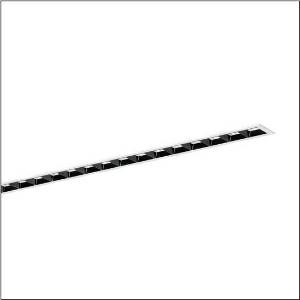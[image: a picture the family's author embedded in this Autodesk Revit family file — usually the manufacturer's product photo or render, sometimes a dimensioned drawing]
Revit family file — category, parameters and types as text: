
# Revit family: silica_r__21_51mx12tctaw_2b1a
name_source: partatom
category: Lighting Fixtures
units: mm (PartAtom-declared; Revit-internal decimal feet)

## family parameters
Cut with Voids When Loaded = No
Host = Face
Light Source = No
Part Type = Normal
Room Calculation Point = No
Round Connector Dimension = Use Diameter
Shared = No

## types (1)
- --- (1 x LED, 9300 lm, 80.4 W, 6500K)
    Apparent Load = 80 VA
    CIE Flux Codes = 84 100 100 100 100
    Color Rendering = 80
    Color Temperature = 6500K
    Default Elevation = 1800 mm
    Description = Silica® 21, office luminaire, primary light control with darklight reflector, of PMMA, black, CAT 2 (L<= 3000cd/m²), light emission: direct distribution, primary light characteristic: symmetric, installation type: recessed, LED, rated luminous flux: 9.300lm, luminous efficacy: 110lm/W, light colour: 8tw, colour temperature: 2700..6500K, with terminal, 3+2-pole, max. 2.5mm², mains connection: 220..240V, AC, 50/60Hz, rated input power: 84.5W, luminaire housing, of aluminium, traffic white (RAL 9016), length: 3.028mm, width: 79mm, height: 53mm, protection rating (complete): IP20, insulation class (complete): insulation class I (protective earthing), certification: CE, permissible operating ambient temperature: 0..+35°C, standard: EN 50419, packaging unit: 1 piece
    Height = 0 mm  [stored 0 ft]
    Lamp = 1 x LED
    Lamp Light Flux = 9300 lm
    Lamp Power = 80.4 W
    Lamp count = 1
    Length = 3027 mm
    Luminous efficacy = 116 lm/W
    Manufacturer = Siteco
    ModVariant = No
    Model = 51MX12TCTAW
    Mounting Place = Ceiling
    Mounting Type = Recessed
    Number of Poles = 1
    OnlyDefault = Yes
    Power Factor = 1
    Product Name = Silica® 21
    Product group = office luminaire | ceiling recessed
    ProductGroupID = 400
    Protection Class = Protection class I
    Protection Degree = IP 20
    RLX_Detail_Level = 1
    RlxData = <blob elided: 59601 chars, md5=60bbec3d>
    Socket = socket
    Standby Power = 0 W
    System Light Flux = 9300 lm
    System Power = 80 W
    Type Comments = individual setting
    Type Image = l_1251632.jpg
    URL = http://relux.com
    VarID = @adj_046257
    Voltage = 0 V
    Weight = 0.00 kg
    Width = 79 mm

note: [stored X ft] marks values corroborated as IEEE doubles in the binary element streams (Revit-internal decimal feet)

## geometry (parser evidence)
native form markers: Blend x4, Sweep x13
no freeform markers — native parametric forms only
